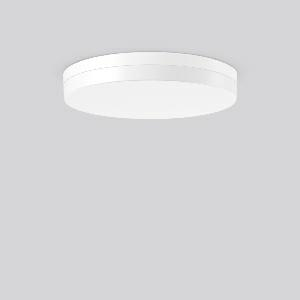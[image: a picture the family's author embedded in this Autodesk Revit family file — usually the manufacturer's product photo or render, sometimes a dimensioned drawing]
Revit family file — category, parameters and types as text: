
# Revit family: flat_slim_round_312677_002_19_bd14
name_source: partatom
category: Lighting Fixtures
units: mm (PartAtom-declared; Revit-internal decimal feet)

## family parameters
Cut with Voids When Loaded = No
Host = Face
Light Source = No
Part Type = Normal
Room Calculation Point = No
Round Connector Dimension = Use Diameter
Shared = No

## types (1)
- MultiLumen 1 830 (1 x LED Modul 830, 3350 lm, 3000)
    Apparent Load = 31 VA
    CIE Flux Codes = 41 71 90 86 100
    Color Rendering = 80
    Color Temperature = 3000
    Default Elevation = 1800 mm
    Height = 75 mm
    Lamp = 1 x LED Modul 830
    Lamp Light Flux = 3350 lm
    Lamp count = 1
    Length = 480 mm
    Lifetime = 50000 h
    Luminous efficacy = 108 lm/W
    Manufacturer = RZB
    ModVariant = No
    Model = 312677.002.19
    Mounting Place = Ceiling
    Mounting Type = Surface mounted
    Number of Poles = 1
    OnlyDefault = Yes
    Power Factor = 1
    Product Name = FLAT SLIM round
    Product group = Surface mounted ceiling and wall luminaires
    ProductGroupID = 305
    Protection Class = Protection class I
    Protection Degree = Degree of protection
    RLX_Detail_Level = 1
    RLX_Emergency_Light_Flux = 0 lm
    RLX_Emergency_Type = 0
    RLX_Emergency_Type_DB = No
    RlxData = <blob elided: 21945 chars, md5=ea978d0a>
    Socket = socket
    Standby Power = 0 W
    System Light Flux = 3350 lm
    System Power = 31 W
    Type Comments = MultiLumen 1 830
    Type Image = 312633.002.jpg
    URL = http://relux.com
    VarID = multilumen_1_830
    Voltage = 0 V
    Weight = 0.00 kg
    Width = 0 mm  [stored 0 ft]

note: [stored X ft] marks values corroborated as IEEE doubles in the binary element streams (Revit-internal decimal feet)

## geometry (parser evidence)
native form markers: Blend x4, Sweep x16
no freeform markers — native parametric forms only
